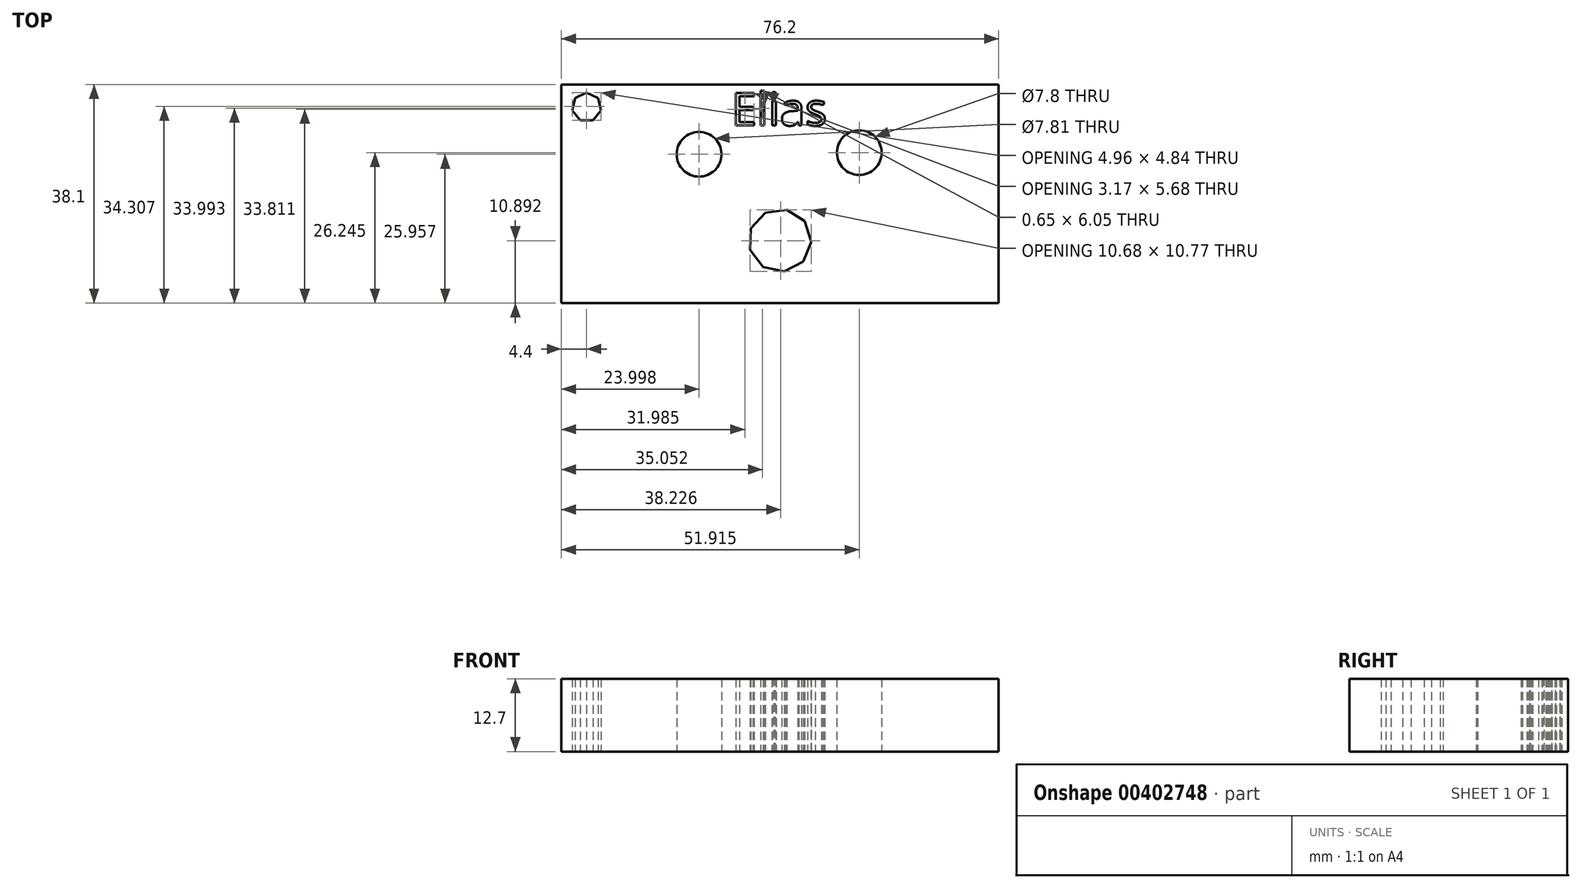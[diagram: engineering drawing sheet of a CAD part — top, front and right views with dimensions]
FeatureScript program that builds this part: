
annotation { "Feature Type Name" : "Feature", "Feature Type Description" : "" }
export const myFeature = defineFeature(function(context is Context, id is Id, definition is map)
    precondition{}
    {
        {
            var Q0;
            Q0=qCreatedBy(makeId("Top.planeOp"),FACE);
            var sketch = newSketch(context, id + "F0", { "sketchPlane" : qUnion([Q0])});
            skLineSegment(sketch, "E0.bottom", {"start": v(-38.1, 19.05) * mm, "end": v(38.1, 19.05) * mm});
            skLineSegment(sketch, "E0.top", {"start": v(-38.1, -19.05) * mm, "end": v(38.1, -19.05) * mm});
            skLineSegment(sketch, "E0.left", {"start": v(-38.1, 19.05) * mm, "end": v(-38.1, -19.05) * mm});
            skLineSegment(sketch, "E0.right", {"start": v(38.1, 19.05) * mm, "end": v(38.1, -19.05) * mm});
            skPoint(sketch, "E0.middle", {"position": v(0, 0) * mm});
            skCircle(sketch, "E1.cCircle", {"center": v(-33.7, 15.13) * mm, "radius": 2.3 * mm, "construction": true});
            skLineSegment(sketch, "E1.0", {"start": v(-32.6, 12.84) * mm, "end": v(-34.8, 12.84) * mm});
            skLineSegment(sketch, "E1.1", {"start": v(-34.8, 12.84) * mm, "end": v(-36.18, 14.56) * mm});
            skLineSegment(sketch, "E1.2", {"start": v(-36.18, 14.56) * mm, "end": v(-35.69, 16.72) * mm});
            skLineSegment(sketch, "E1.3", {"start": v(-35.69, 16.72) * mm, "end": v(-33.7, 17.68) * mm});
            skLineSegment(sketch, "E1.4", {"start": v(-33.7, 17.68) * mm, "end": v(-31.71, 16.72) * mm});
            skLineSegment(sketch, "E1.5", {"start": v(-31.71, 16.72) * mm, "end": v(-31.22, 14.56) * mm});
            skLineSegment(sketch, "E1.6", {"start": v(-31.22, 14.56) * mm, "end": v(-32.6, 12.84) * mm});
            skPoint(sketch, "E1.0.midPoint", {"position": v(-33.7, 12.84) * mm});
            skCircle(sketch, "E2", {"center": v(-14.1, 6.9) * mm, "radius": 3.9 * mm});
            skText(sketch, "E3", { "text": "Elias", "fontName": "OpenSans-Regular.ttf"});
            skCircle(sketch, "E4", {"center": v(13.81, 7.2) * mm, "radius": 3.9 * mm});
            skCircle(sketch, "E5.cCircle", {"center": v(0, -8.12) * mm, "radius": 5.47 * mm, "construction": true});
            skLineSegment(sketch, "E5.0", {"start": v(4.04, -11.8) * mm, "end": v(0.73, -13.54) * mm});
            skLineSegment(sketch, "E5.1", {"start": v(0.73, -13.54) * mm, "end": v(-2.93, -12.74) * mm});
            skLineSegment(sketch, "E5.2", {"start": v(-2.93, -12.74) * mm, "end": v(-5.22, -9.77) * mm});
            skLineSegment(sketch, "E5.3", {"start": v(-5.22, -9.77) * mm, "end": v(-5.06, -6.03) * mm});
            skLineSegment(sketch, "E5.4", {"start": v(-5.06, -6.03) * mm, "end": v(-2.54, -3.27) * mm});
            skLineSegment(sketch, "E5.5", {"start": v(-2.54, -3.27) * mm, "end": v(1.17, -2.77) * mm});
            skLineSegment(sketch, "E5.6", {"start": v(1.17, -2.77) * mm, "end": v(4.34, -4.78) * mm});
            skLineSegment(sketch, "E5.7", {"start": v(4.34, -4.78) * mm, "end": v(5.47, -8.35) * mm});
            skLineSegment(sketch, "E5.8", {"start": v(5.47, -8.35) * mm, "end": v(4.04, -11.8) * mm});
            const initialGuessF0  = {"E3": [-0.00848, 0.01192, 1, 0, 0.00573]};
            skSetInitialGuess(sketch, initialGuessF0);
            skSolve(sketch);
        }
        {
            var Q0;
            Q0 = qSketchRegion(id + "F0", true);
            extrude(context, id + "F1", {"entities" : qUnion([Q0]), "depth" : 12.7 * mm});
        }
    });
